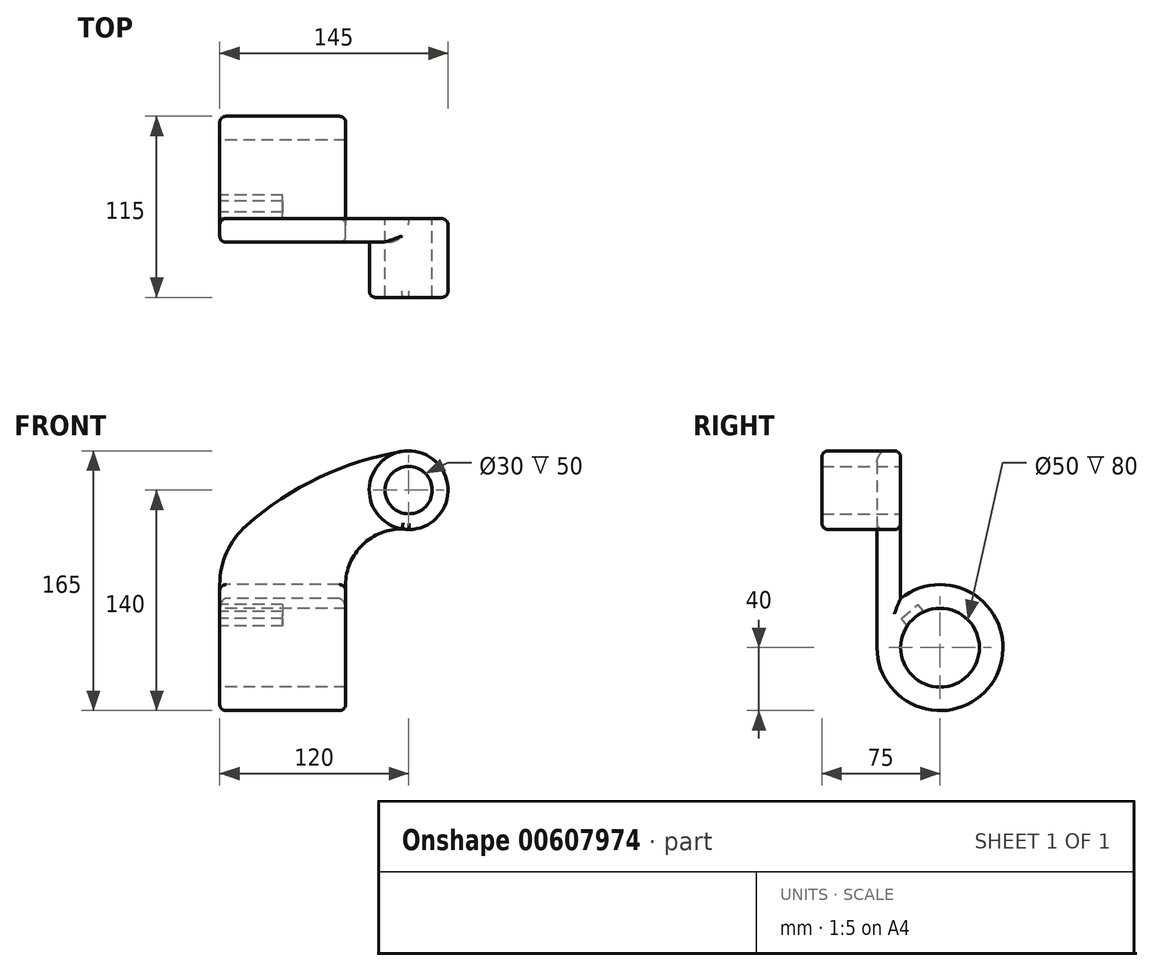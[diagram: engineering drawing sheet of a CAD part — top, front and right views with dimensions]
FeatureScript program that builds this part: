
annotation { "Feature Type Name" : "Feature", "Feature Type Description" : "" }
export const myFeature = defineFeature(function(context is Context, id is Id, definition is map)
    precondition{}
    {
        {
            var Q0;
            Q0=qCreatedBy(makeId("Front.planeOp"),FACE);
            var sketch = newSketch(context, id + "F0", { "sketchPlane" : qUnion([Q0])});
            skLineSegment(sketch, "E0", {"start": v(-99.17, 0) * mm, "end": v(0, 0) * mm, "construction": true});
            skLineSegment(sketch, "E1", {"start": v(-80, 25) * mm, "end": v(0, 25) * mm});
            skLineSegment(sketch, "E2", {"start": v(0, 40) * mm, "end": v(-80, 40) * mm});
            skLineSegment(sketch, "E3", {"start": v(-80, 40) * mm, "end": v(-80, 25) * mm});
            skLineSegment(sketch, "E4", {"start": v(0, 40) * mm, "end": v(0, 25) * mm});
            skCircle(sketch, "E5", {"center": v(40, 100) * mm, "radius": 15 * mm});
            skCircle(sketch, "E6", {"center": v(40, 100) * mm, "radius": 25 * mm});
            skLineSegment(sketch, "E7", {"start": v(40, 100) * mm, "end": v(40, 0) * mm});
            skLineSegment(sketch, "E8", {"start": v(40, 0) * mm, "end": v(37.86, -0.52) * mm});
            skArc(sketch, "E9", {"start": v(40, 75) * mm, "mid": v(12.06, 66.58) * mm, "end": v(0, 40) * mm});
            skArc(sketch, "E10", {"start": v(-80, 40) * mm, "mid": v(-75.57, 60.58) * mm, "end": v(-63.05, 77.52) * mm});
            skArc(sketch, "E11", {"start": v(-63.05, 77.52) * mm, "mid": v(-16.9, 107.99) * mm, "end": v(35.84, 124.65) * mm});
            skLineSegment(sketch, "E12.top", {"start": v(-80, 0) * mm, "end": v(0, 0) * mm});
            skLineSegment(sketch, "E12.left", {"start": v(-80, 25) * mm, "end": v(-80, 0) * mm});
            skLineSegment(sketch, "E12.right", {"start": v(0, 25) * mm, "end": v(0, 0) * mm});
            skSolve(sketch);
        }
        {
            var Q0;
            Q0=makeQuery(id+"F0.imprint","IMPRINT",FACE,{"disambiguationData":[TD([[makeQuery(id+"F0.imprint","IMPRINT",EDGE,{"derivedFrom":sQuery(id+"F0.wireOp",EDGE,"E2")}),1.0]])]});
            var Q1;
            Q1=sQuery(id+"F0.wireOp",EDGE,"E12.top");
            revolve(context, id + "F1", {"entities" : qUnion([Q0]), "axis" : qUnion([Q1]), "revolveType" : RevolveType.FULL});
        }
        {
            var Q0;
            {var subQ1=sQuery(id+"F0.wireOp",EDGE,"E2");Q0=makeQuery(id+"F0.imprint","IMPRINT",FACE,{"disambiguationData":[TD([[makeQuery(id+"F0.imprint","IMPRINT",EDGE,{"derivedFrom":subQ1}),-1.0]])]});}
            var Q1;
            Q1=makeQuery(id+"F0.imprint","IMPRINT",FACE,{"disambiguationData":[TD([[makeQuery(id+"F0.imprint","IMPRINT",EDGE,{"derivedFrom":sQuery(id+"F0.wireOp",EDGE,"E1")}),-1.0]])]});
            var Q2;
            Q2=makeQuery(id+"F0.imprint","IMPRINT",FACE,{"disambiguationData":[TD([[makeQuery(id+"F0.imprint","IMPRINT",EDGE,{"derivedFrom":sQuery(id+"F0.wireOp",EDGE,"E2")}),1.0]])]});
            extrude(context, id + "F2", {"entities" : qUnion([Q0, Q1, Q2]), "operationType" : NewBodyOperationType.ADD, "depth" : 40 * mm, "offsetDistance" : 25 * mm, "hasSecondDirection" : true, "secondDirectionOppositeDirection" : false, "secondDirectionDepth" : 25 * mm});
        }
        {
            var Q0;
            Q0=makeQuery(id+"F0.imprint","IMPRINT",FACE,{"disambiguationData":[TD([[makeQuery(id+"F0.imprint","IMPRINT",EDGE,{"derivedFrom":sQuery(id+"F0.wireOp",EDGE,"E5")}),-1.0]])]});
            extrude(context, id + "F3", {"entities" : qUnion([Q0]), "operationType" : NewBodyOperationType.ADD, "depth" : 75 * mm, "offsetDistance" : 25 * mm, "hasSecondDirection" : true, "secondDirectionOppositeDirection" : false, "secondDirectionDepth" : 25 * mm});
        }
        {
            var Q0;
            Q0=makeQuery(id+"F3.opExtrude","CAP_EDGE",EDGE,{"disambiguationData":[OSD([sQuery(id+"F0.wireOp",EDGE,"E6")])],"isStart":false});
            fillet(context, id + "F4", {"entities" : qUnion([Q0]), "radius" : 4 * mm, "tangentPropagation" : true, "allowEdgeOverflow" : false});
        }
        {
            var Q0;
            Q0=makeQuery(id+"F2.opExtrude","CAP_EDGE",EDGE,{"disambiguationData":[OSD([sQuery(id+"F0.wireOp",EDGE,"E11")])],"isStart":false});
            fillet(context, id + "F5", {"entities" : qUnion([Q0]), "radius" : 4 * mm, "tangentPropagation" : true, "allowEdgeOverflow" : false});
        }
        {
            var Q0;
            Q0=makeQuery(id+"F1.opRevolve","SWEPT_EDGE",EDGE,{"disambiguationData":[OSD([sQuery(id+"F0.wireOp",EDGE,"E2"),sQuery(id+"F0.wireOp",EDGE,"E4"),sQuery(id+"F0.wireOp",EDGE,"E9")])]});
            fillet(context, id + "F6", {"entities" : qUnion([Q0]), "radius" : 4 * mm, "tangentPropagation" : true, "allowEdgeOverflow" : false});
        }
        {
            var Q0;
            {var subQ0=sQuery(id+"F0.wireOp",EDGE,"E9");Q0=makeQuery(id+"F3.boolean.opBoolean","MERGE",EDGE,{"derivedFrom":[makeQuery(id+"F2.opExtrude","CAP_EDGE",EDGE,{"disambiguationData":[OSD([subQ0])],"isStart":true}),makeQuery(id+"F3.opExtrude","CAP_EDGE",EDGE,{"disambiguationData":[OSD([subQ0])],"isStart":true})]});}
            fillet(context, id + "F7", {"entities" : qUnion([Q0]), "radius" : 4 * mm, "tangentPropagation" : true, "allowEdgeOverflow" : false});
        }
        {
            var Q0;
            Q0=makeQuery(id+"F2.opExtrude","CAP_EDGE",EDGE,{"disambiguationData":[OSD([sQuery(id+"F0.wireOp",EDGE,"E11")])],"isStart":true});
            fillet(context, id + "F8", {"entities" : qUnion([Q0]), "radius" : 4 * mm, "tangentPropagation" : true, "allowEdgeOverflow" : false});
        }
        {
            var Q0;
            {var subQ0=sQuery(id+"F0.wireOp",EDGE,"E3");Q0=makeQuery(id+"F2.boolean.opBoolean","MERGE",FACE,{"derivedFrom":[makeQuery(id+"F1.opRevolve","SWEPT_FACE",FACE,{"disambiguationData":[OSD([subQ0])]}),makeQuery(id+"F2.opExtrude","SWEPT_FACE",FACE,{"disambiguationData":[OSD([subQ0,sQuery(id+"F0.wireOp",EDGE,"E12.left")])]})]});}
            var sketch = newSketch(context, id + "F9", { "sketchPlane" : qUnion([Q0])});
            skLineSegment(sketch, "E13.bottom", {"start": v(13.92, 27.48) * mm, "end": v(24.65, 18.48) * mm});
            skLineSegment(sketch, "E13.top", {"start": v(-5.36, 4.5) * mm, "end": v(5.36, -4.5) * mm});
            skLineSegment(sketch, "E13.left", {"start": v(13.92, 27.48) * mm, "end": v(-5.36, 4.5) * mm});
            skLineSegment(sketch, "E13.right", {"start": v(24.65, 18.48) * mm, "end": v(5.36, -4.5) * mm});
            skSolve(sketch);
        }
        {
            var Q0;
            {var subQ0=sQuery(id+"F9.wireOp",EDGE,"E13.bottom");Q0=makeQuery(id+"F9.imprint","IMPRINT",FACE,{"disambiguationData":[TD([[makeQuery(id+"F9.imprint","IMPRINT",EDGE,{"derivedFrom":subQ0}),-1.0]])]});}
            extrude(context, id + "F10", {"entities" : qUnion([Q0]), "operationType" : NewBodyOperationType.REMOVE, "endBound" : BoundingType.SYMMETRIC, "oppositeDirection" : true, "depth" : 80 * mm, "offsetDistance" : 25 * mm});
        }
    });
